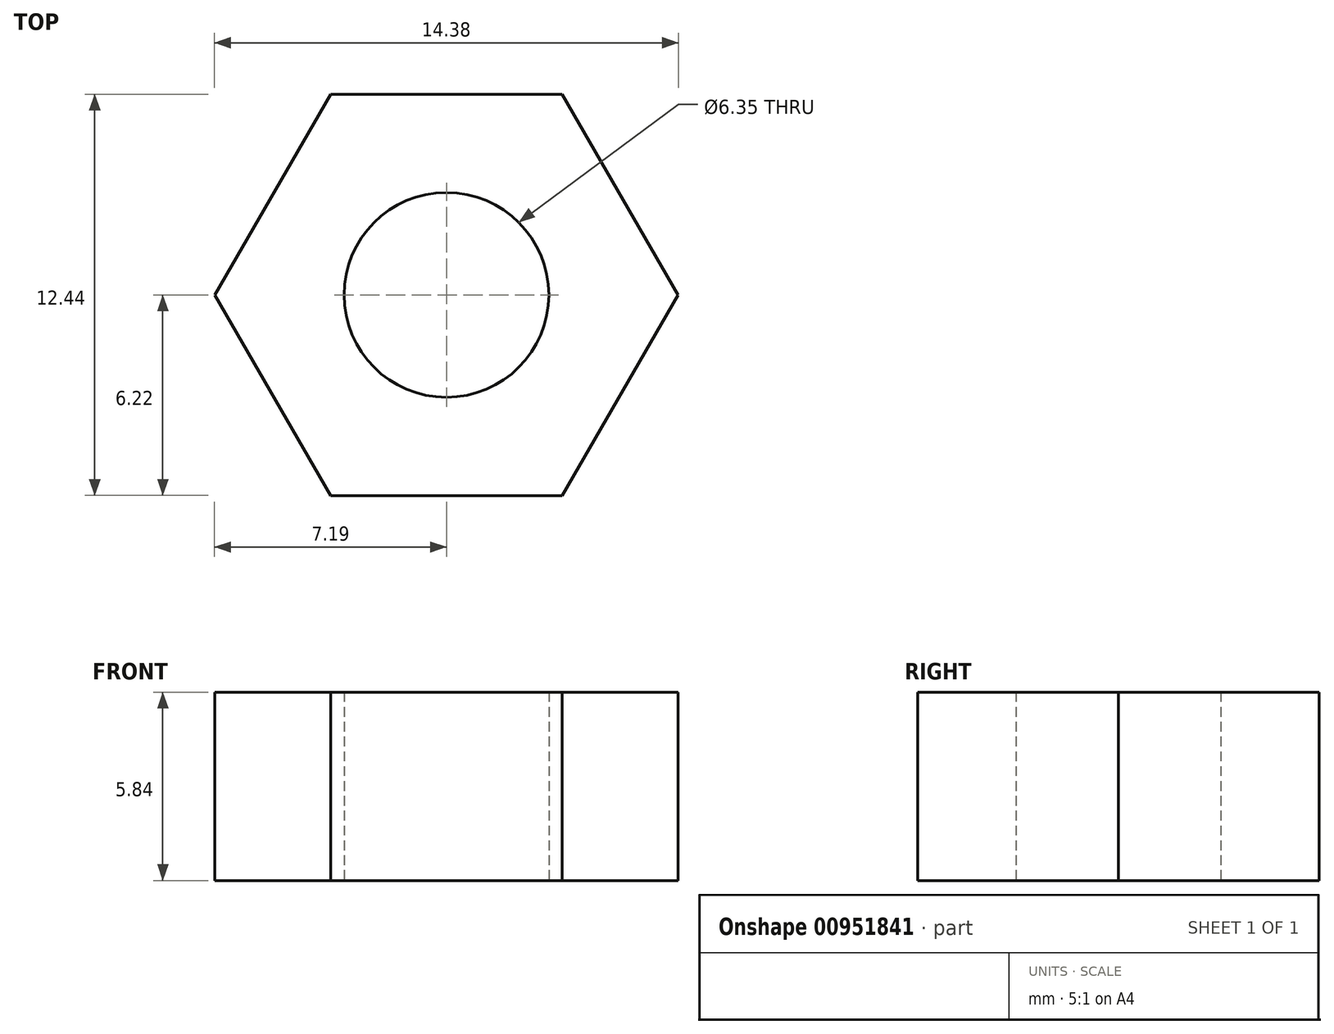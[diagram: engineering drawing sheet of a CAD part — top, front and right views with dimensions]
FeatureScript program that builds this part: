
annotation { "Feature Type Name" : "Feature", "Feature Type Description" : "" }
export const myFeature = defineFeature(function(context is Context, id is Id, definition is map)
    precondition{}
    {
        {
            var Q0;
            Q0=qCreatedBy(makeId("Top.planeOp"),FACE);
            var sketch = newSketch(context, id + "F0", { "sketchPlane" : qUnion([Q0])});
            skCircle(sketch, "E0.cCircle", {"center": v(0, 0) * mm, "radius": 6.22 * mm, "construction": true});
            skLineSegment(sketch, "E0.0", {"start": v(3.6, -6.22) * mm, "end": v(-3.6, -6.22) * mm});
            skLineSegment(sketch, "E0.1", {"start": v(-3.6, -6.22) * mm, "end": v(-7.19, 0) * mm});
            skLineSegment(sketch, "E0.2", {"start": v(-7.19, 0) * mm, "end": v(-3.6, 6.22) * mm});
            skLineSegment(sketch, "E0.3", {"start": v(-3.6, 6.22) * mm, "end": v(3.6, 6.22) * mm});
            skLineSegment(sketch, "E0.4", {"start": v(3.6, 6.22) * mm, "end": v(7.19, 0) * mm});
            skLineSegment(sketch, "E0.5", {"start": v(7.19, 0) * mm, "end": v(3.6, -6.22) * mm});
            skPoint(sketch, "E0.0.midPoint", {"position": v(0, -6.22) * mm});
            skCircle(sketch, "E1", {"center": v(0, 0) * mm, "radius": 3.18 * mm});
            skSolve(sketch);
        }
        {
            var Q0;
            Q0 = qSketchRegion(id + "F0", true);
            extrude(context, id + "F1", {"entities" : qUnion([Q0]), "endBound" : BoundingType.SYMMETRIC, "depth" : 5.84 * mm, "offsetDistance" : 25.4 * mm});
        }
    });
